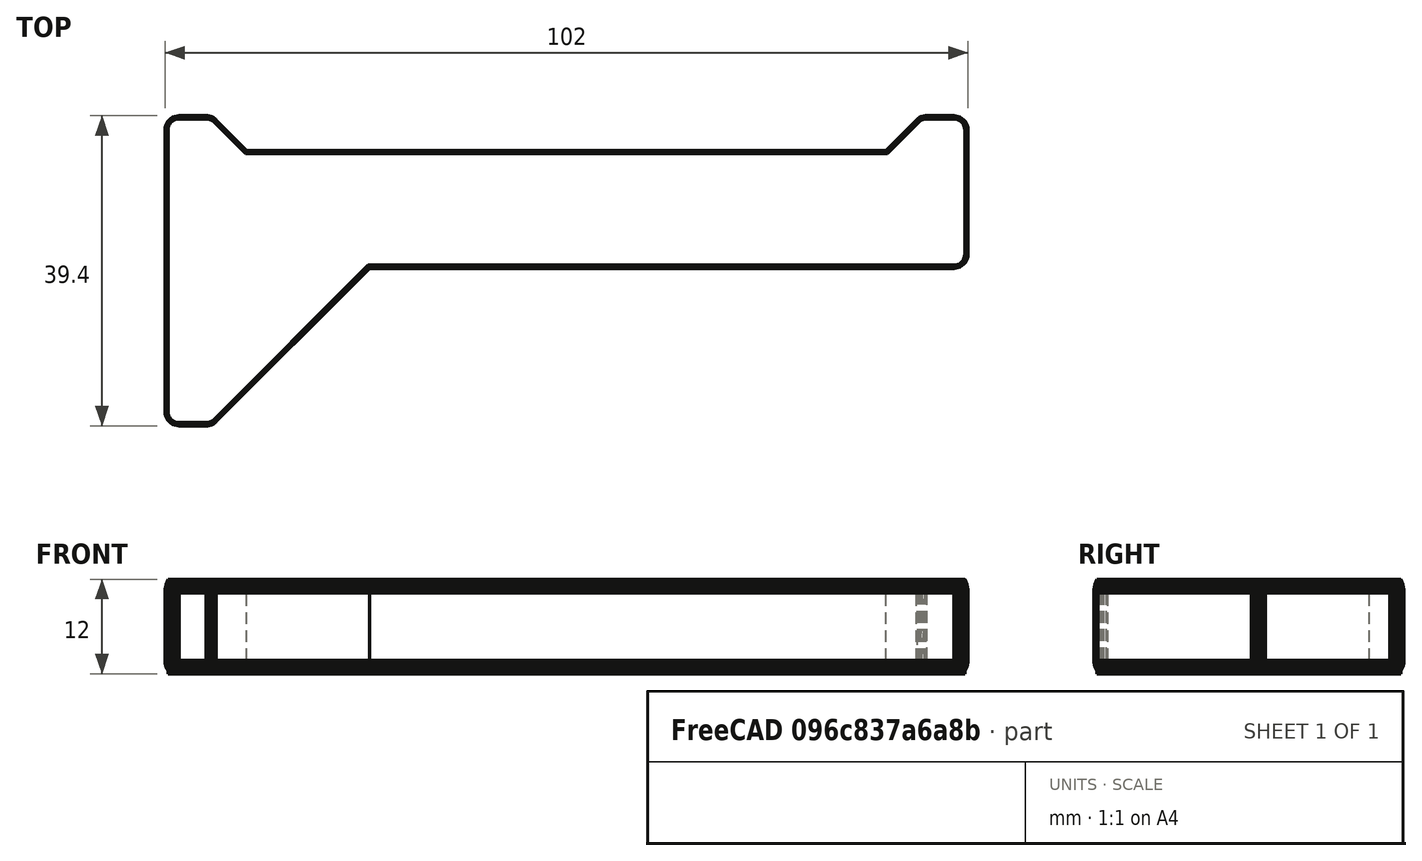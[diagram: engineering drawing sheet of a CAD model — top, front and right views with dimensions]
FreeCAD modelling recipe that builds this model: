
FCSTD DOCUMENT  (FreeCAD 0.18R14555 (Git shallow))
Label: bear-mera-Z-helper-4mm-shorter
License: All rights reserved
LicenseURL: http://en.wikipedia.org/wiki/All_rights_reserved
objects: Part::Feature×5, Part::Box×2, Mesh::Feature×1, Part::Cut×1, Part::MultiCommon×1, Part::MultiFuse×1
note: 10 computed .brp shape members not serialized (recipe doc carries the construction recipe); baked Part::Feature solids carry a one-line shape summary decoded from their .brp

FEATURE [Mesh::Feature] build_helper_z
FEATURE [Part::Feature] build_helper_z001
  shape: bbox 106 x 39.4 x 12 mm, 2268 faces, 0 solids (baked)
FEATURE [Part::Feature] build_helper_z001001  label="build_helper_z002"
  shape: bbox 106 x 39.4 x 12 mm, 1608 faces, 0 solids (baked)
FEATURE [Part::Feature] build_helper_z001001_solid  label="build_helper_z002 (Solid)"
  shape: bbox 106 x 39.4 x 12 mm, 1608 faces (baked)
FEATURE [Part::Box] Box  label="Cube"
  AttacherType = Attacher::AttachEngine3D
  Height = 15
  Length = 55
  Placement = pos=(-4,-43,0) rot=(0,0,1;0rad)
  Width = 49
FEATURE [Part::Feature] build_helper_z001001_solid001  label="build_helper_z002 (Solid)001"
  shape: bbox 106 x 39.4 x 12 mm, 1608 faces (baked)
FEATURE [Part::Box] Box001  label="Cube001"
  AttacherType = Attacher::AttachEngine3D
  Height = 15
  Length = 55
  Placement = pos=(-4,-43,0) rot=(0,0,1;0rad)
  Width = 49
FEATURE [Part::Cut] Cut
  Base = -> build_helper_z001001_solid
  Tool = -> Box
FEATURE [Part::MultiCommon] Common
  Placement = pos=(4,0,0) rot=(0,0,1;0rad)
  Shapes = -> [Box001,build_helper_z001001_solid001]
FEATURE [Part::MultiFuse] Fusion
  Shapes = -> [Cut,Common]
FEATURE [Part::Feature] Fusion001  label="4mm"
  shape: bbox 102 x 39.4 x 12 mm, 1616 faces (baked)
